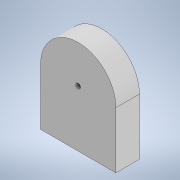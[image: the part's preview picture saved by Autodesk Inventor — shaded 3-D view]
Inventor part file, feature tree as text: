
AUTODESK INVENTOR PART (.ipt)
format: ipt  version: 2022 (Build 260153000, 153)  size: 104,448 bytes
history: native  units: mm
features: extrude x2, sketch x2, fillet x1
ambient origin geometry x8: Origin, YZ Plane, XZ Plane, XY Plane, X Axis, Y Axis, Z Axis, Center Point
bodies: Solid1 (feature_tree)
feature tree (5):
  extrude  "Extrusion1"  Depth=25.0mm
  fillet  "Fillet1"  Radius=100.0mm
  extrude  "Extrusion2"  Depth=40.0mm
  sketch  "Sketch1"  dims[d0=80.0mm d1=25.0mm d2=100.0mm d3=0.0mm]
  sketch  "Sketch2"  dims[d4=40.0mm d5=5.0mm d6=100.0mm d7=0.0mm]
